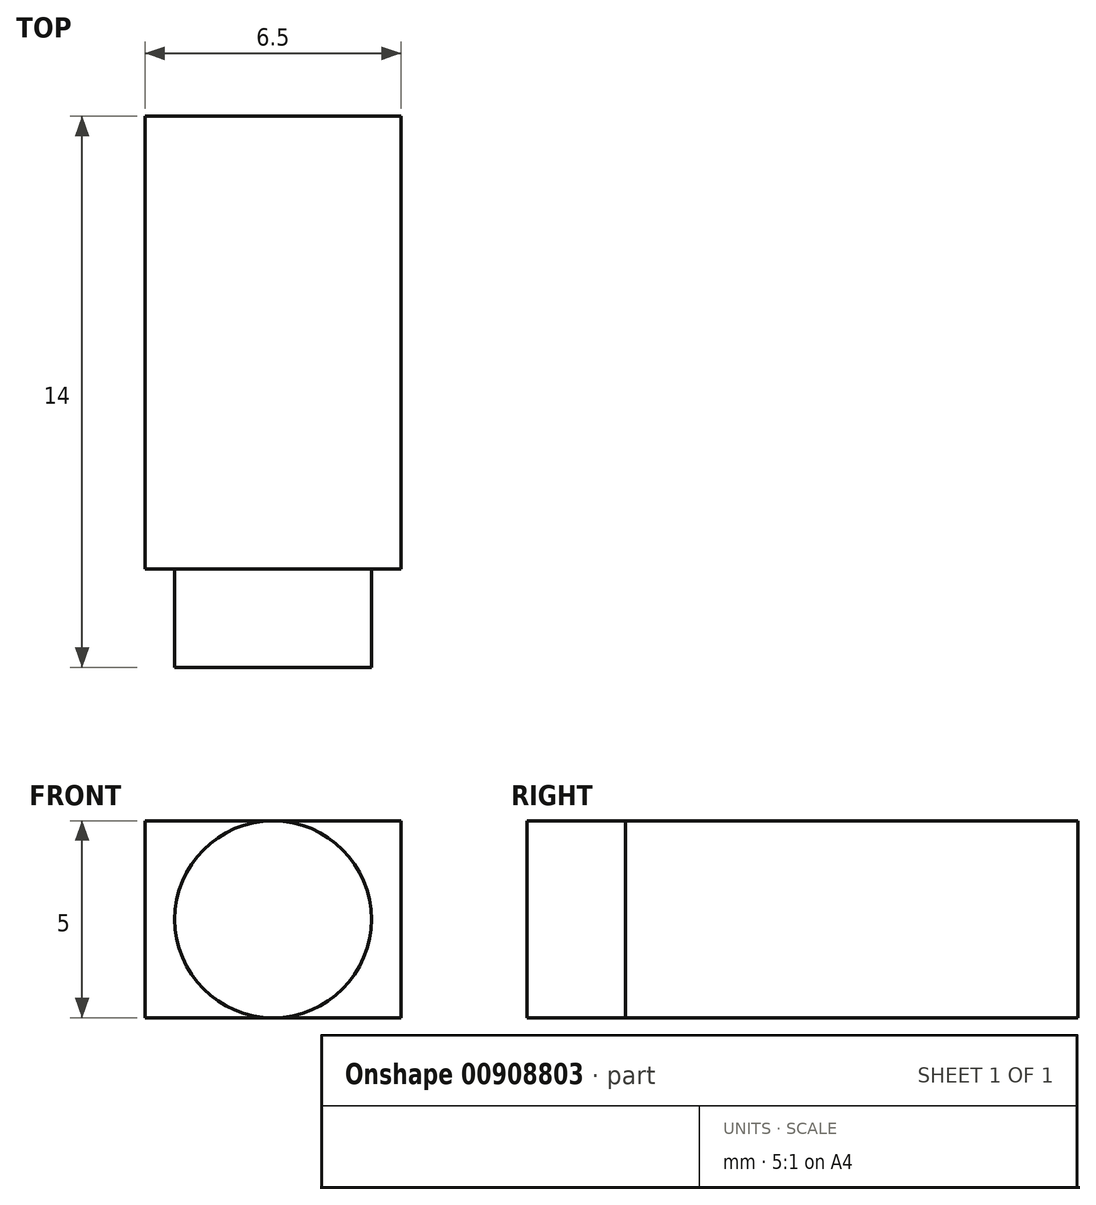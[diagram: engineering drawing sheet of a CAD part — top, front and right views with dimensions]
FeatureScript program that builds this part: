
annotation { "Feature Type Name" : "Feature", "Feature Type Description" : "" }
export const myFeature = defineFeature(function(context is Context, id is Id, definition is map)
    precondition{}
    {
        {
            var Q0;
            Q0=qCreatedBy(makeId("Front.planeOp"),FACE);
            var sketch = newSketch(context, id + "F0", { "sketchPlane" : qUnion([Q0])});
            skLineSegment(sketch, "E0.bottom", {"start": v(3.25, -2.5) * mm, "end": v(-3.25, -2.5) * mm});
            skLineSegment(sketch, "E0.top", {"start": v(3.25, 2.5) * mm, "end": v(-3.25, 2.5) * mm});
            skLineSegment(sketch, "E0.left", {"start": v(3.25, -2.5) * mm, "end": v(3.25, 2.5) * mm});
            skLineSegment(sketch, "E0.right", {"start": v(-3.25, -2.5) * mm, "end": v(-3.25, 2.5) * mm});
            skPoint(sketch, "E0.middle", {"position": v(0, 0) * mm});
            skSolve(sketch);
        }
        {
            var Q0;
            Q0=qSketchRegion(id+"F0",true);
            extrude(context, id + "F1", {"entities" : qUnion([Q0]), "depth" : 11.5 * mm});
        }
        {
            var Q0;
            Q0=makeQuery(id+"F1.opExtrude","CAP_FACE",FACE,{"disambiguationData":[OSD([sQuery(id+"F0.wireOp",EDGE,"E0.bottom"),sQuery(id+"F0.wireOp",EDGE,"E0.top"),sQuery(id+"F0.wireOp",EDGE,"E0.left"),sQuery(id+"F0.wireOp",EDGE,"E0.right")])],"isStart":false});
            var sketch = newSketch(context, id + "F2", { "sketchPlane" : qUnion([Q0])});
            skCircle(sketch, "E1", {"center": v(0, 0) * mm, "radius": 2.5 * mm});
            skSolve(sketch);
        }
        {
            var Q0;
            Q0=qSketchRegion(id+"F2",true);
            extrude(context, id + "F3", {"entities" : qUnion([Q0]), "operationType" : NewBodyOperationType.ADD, "depth" : 2.5 * mm});
        }
    });
